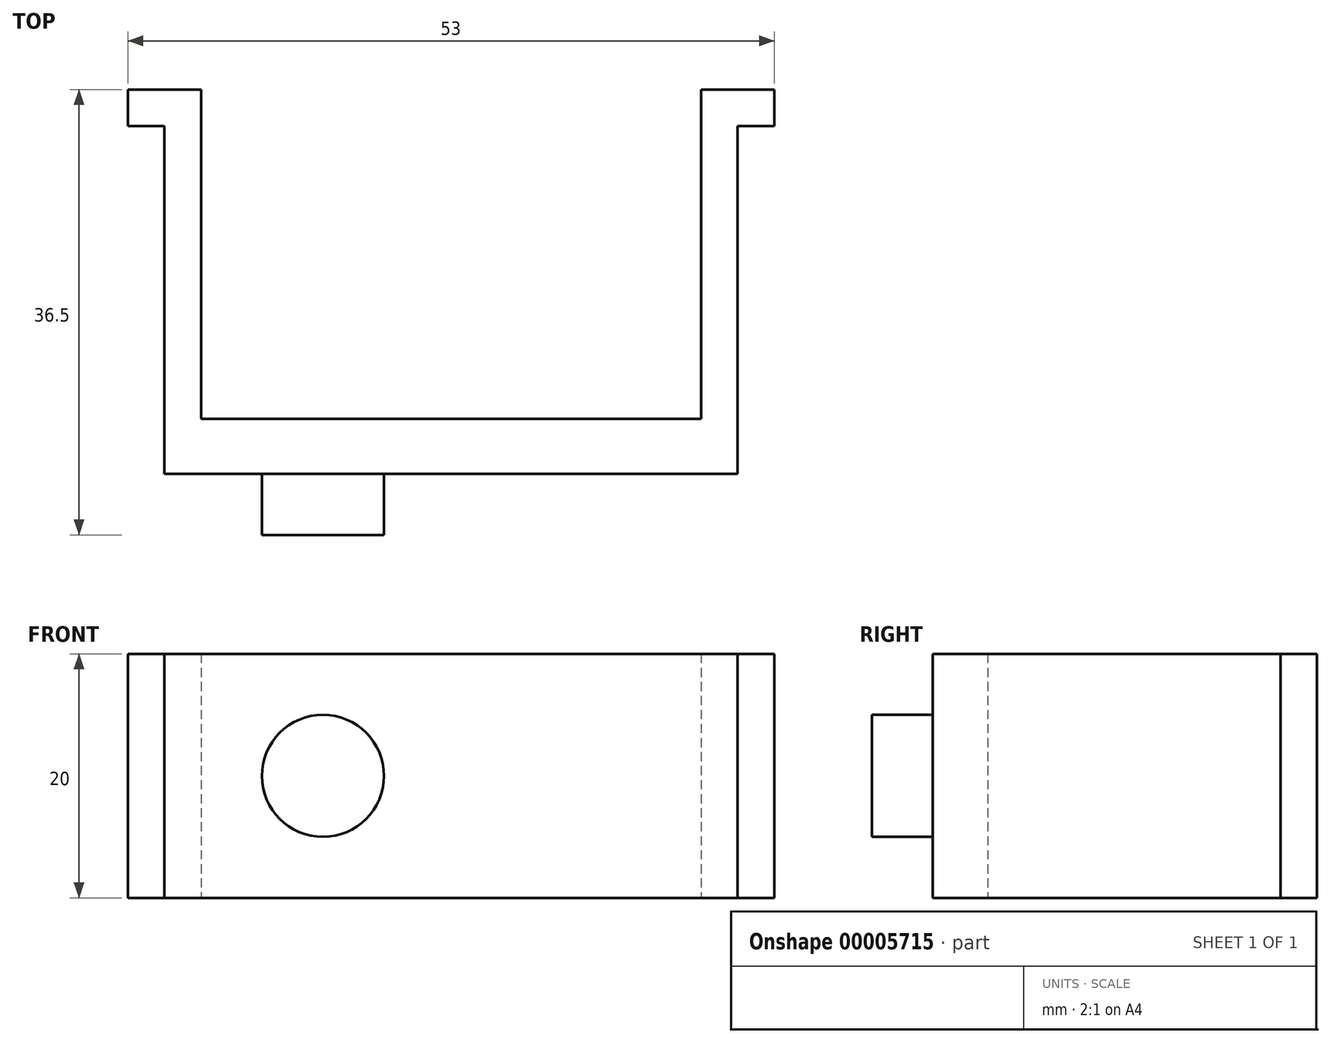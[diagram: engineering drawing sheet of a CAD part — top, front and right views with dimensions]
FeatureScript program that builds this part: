
annotation { "Feature Type Name" : "Feature", "Feature Type Description" : "" }
export const myFeature = defineFeature(function(context is Context, id is Id, definition is map)
    precondition{}
    {
        {
            var Q0;
            Q0=qCreatedBy(makeId("Top.planeOp"),FACE);
            var sketch = newSketch(context, id + "F0", { "sketchPlane" : qUnion([Q0])});
            skLineSegment(sketch, "E0.left", {"start": v(-20.5, -15.1) * mm, "end": v(-20.5, -27) * mm});
            skLineSegment(sketch, "E1.top", {"start": v(-23.5, -31.5) * mm, "end": v(-20.5, -31.5) * mm});
            skLineSegment(sketch, "E1.left", {"start": v(-23.5, -3) * mm, "end": v(-23.5, -31.5) * mm});
            skLineSegment(sketch, "E2.top", {"start": v(-26.5, -3) * mm, "end": v(-23.5, -3) * mm});
            skLineSegment(sketch, "E2.left", {"start": v(-26.5, 0) * mm, "end": v(-26.5, -3) * mm});
            skLineSegment(sketch, "E3", {"start": v(-20.5, -27) * mm, "end": v(0, -27) * mm});
            skLineSegment(sketch, "E4", {"start": v(-26.5, 0) * mm, "end": v(-20.5, 0) * mm});
            skLineSegment(sketch, "E5", {"start": v(-20.5, -15.1) * mm, "end": v(-20.5, 0) * mm});
            skLineSegment(sketch, "E6", {"start": v(0, -27) * mm, "end": v(0, -31.5) * mm});
            skPoint(sketch, "E7.start.orphan", {"position": v(-1.76, 0) * mm});
            skPoint(sketch, "E0.right.start.orphan", {"position": v(-1.76, -3) * mm});
            skPoint(sketch, "E8", {"position": v(-20.5, -31.5) * mm});
            skLineSegment(sketch, "E9", {"start": v(-20.5, -31.5) * mm, "end": v(0, -31.5) * mm});
            skSolve(sketch);
        }
        {
            var Q0;
            Q0=makeQuery(id+"F0.imprint","IMPRINT",FACE,{"disambiguationData":[TD([[makeQuery(id+"F0.imprint","IMPRINT",EDGE,{"derivedFrom":sQuery(id+"F0.wireOp",EDGE,"E0.left")}),-1.0]])]});
            extrude(context, id + "F1", {"entities" : qUnion([Q0]), "depth" : 20 * mm});
        }
        {
            var Q0;
            Q0=makeQuery(id+"F1.opExtrude","SWEPT_BODY",BODY,{"disambiguationData":[OSD([sQuery(id+"F0.wireOp",EDGE,"E0.left"),sQuery(id+"F0.wireOp",EDGE,"E1.top"),sQuery(id+"F0.wireOp",EDGE,"E1.left"),sQuery(id+"F0.wireOp",EDGE,"E2.top"),sQuery(id+"F0.wireOp",EDGE,"E2.left"),sQuery(id+"F0.wireOp",EDGE,"E3"),sQuery(id+"F0.wireOp",EDGE,"E4"),sQuery(id+"F0.wireOp",EDGE,"E5"),sQuery(id+"F0.wireOp",EDGE,"E6"),sQuery(id+"F0.wireOp",EDGE,"E9")])]});
            var Q1;
            Q1=qCreatedBy(makeId("Right.planeOp"),FACE);
            mirror(context, id + "F2", {"entities" : qUnion([Q0]), "mirrorPlane" : qUnion([Q1])});
        }
        {
            var Q0;
            Q0=makeQuery(id+"F1.opExtrude","SWEPT_BODY",BODY,{"disambiguationData":[OSD([sQuery(id+"F0.wireOp",EDGE,"E0.left"),sQuery(id+"F0.wireOp",EDGE,"E1.top"),sQuery(id+"F0.wireOp",EDGE,"E1.left"),sQuery(id+"F0.wireOp",EDGE,"E2.top"),sQuery(id+"F0.wireOp",EDGE,"E2.left"),sQuery(id+"F0.wireOp",EDGE,"E3"),sQuery(id+"F0.wireOp",EDGE,"E4"),sQuery(id+"F0.wireOp",EDGE,"E5"),sQuery(id+"F0.wireOp",EDGE,"E6"),sQuery(id+"F0.wireOp",EDGE,"E9")])]});
            var Q1;
            Q1=makeQuery(id+"F2.opPattern","COPY",BODY,{"derivedFrom":makeQuery(id+"F1.opExtrude","SWEPT_BODY",BODY,{"disambiguationData":[OSD([sQuery(id+"F0.wireOp",EDGE,"E0.left"),sQuery(id+"F0.wireOp",EDGE,"E1.top"),sQuery(id+"F0.wireOp",EDGE,"E1.left"),sQuery(id+"F0.wireOp",EDGE,"E2.top"),sQuery(id+"F0.wireOp",EDGE,"E2.left"),sQuery(id+"F0.wireOp",EDGE,"E3"),sQuery(id+"F0.wireOp",EDGE,"E4"),sQuery(id+"F0.wireOp",EDGE,"E5"),sQuery(id+"F0.wireOp",EDGE,"E6"),sQuery(id+"F0.wireOp",EDGE,"E9")])]}),"instanceName":"1"});
            booleanBodies(context, id + "F3", {"operationType" : BooleanOperationType.UNION, "tools" : qUnion([Q0, Q1])});
        }
        {
            var Q0;
            {var subQ0=makeQuery(id+"F1.opExtrude","SWEPT_FACE",FACE,{"disambiguationData":[OSD([sQuery(id+"F0.wireOp",EDGE,"E1.top"),sQuery(id+"F0.wireOp",EDGE,"E9")])]});Q0=makeQuery(id+"F3.opBoolean","MERGE",FACE,{"derivedFrom":[subQ0,makeQuery(id+"F2.opPattern","COPY",FACE,{"derivedFrom":subQ0,"instanceName":"1"})]});}
            var sketch = newSketch(context, id + "F4", { "sketchPlane" : qUnion([Q0])});
            skCircle(sketch, "E10", {"center": v(-10.5, 10) * mm, "radius": 5 * mm});
            skPoint(sketch, "E11", {"position": v(-23.5, 10) * mm});
            skSolve(sketch);
        }
        {
            var Q0;
            Q0=makeQuery(id+"F4.imprint","IMPRINT",FACE,{"disambiguationData":[TD([[makeQuery(id+"F4.imprint","IMPRINT",EDGE,{"derivedFrom":sQuery(id+"F4.wireOp",EDGE,"E10")}),1.0]])]});
            extrude(context, id + "F5", {"entities" : qUnion([Q0]), "operationType" : NewBodyOperationType.ADD, "depth" : 5 * mm});
        }
    });
